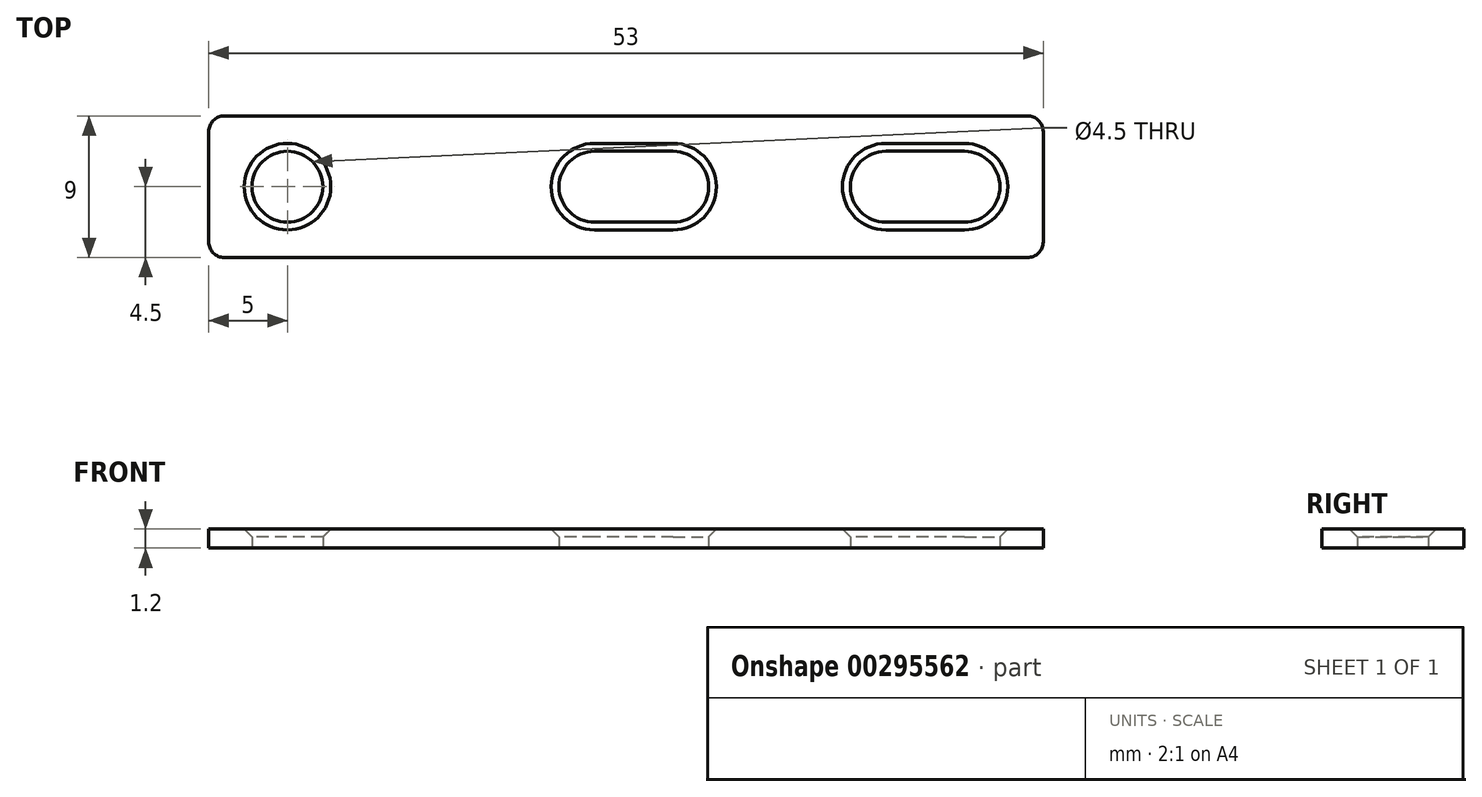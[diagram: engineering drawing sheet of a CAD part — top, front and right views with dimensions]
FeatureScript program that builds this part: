
annotation { "Feature Type Name" : "Feature", "Feature Type Description" : "" }
export const myFeature = defineFeature(function(context is Context, id is Id, definition is map)
    precondition{}
    {
        {
            var Q0;
            Q0=qCreatedBy(makeId("Top.planeOp"),FACE);
            var sketch = newSketch(context, id + "F0", { "sketchPlane" : qUnion([Q0])});
            skLineSegment(sketch, "E0.bottom", {"start": v(26.5, 4.5) * mm, "end": v(-26.5, 4.5) * mm});
            skLineSegment(sketch, "E0.top", {"start": v(26.5, -4.5) * mm, "end": v(-26.5, -4.5) * mm});
            skLineSegment(sketch, "E0.left", {"start": v(26.5, 4.5) * mm, "end": v(26.5, -4.5) * mm});
            skLineSegment(sketch, "E0.right", {"start": v(-26.5, 4.5) * mm, "end": v(-26.5, -4.5) * mm});
            skPoint(sketch, "E0.middle", {"position": v(0, 0) * mm});
            skCircle(sketch, "E1", {"center": v(-21.5, 0) * mm, "radius": 2.25 * mm});
            skPoint(sketch, "E1.centerSnap0", {"position": v(-26.5, 0) * mm});
            skLineSegment(sketch, "E2", {"start": v(-2, 0) * mm, "end": v(3, 0) * mm, "construction": true});
            skLineSegment(sketch, "E3", {"start": v(-26.5, 0) * mm, "end": v(-21.5, 0) * mm, "construction": true});
            skLineSegment(sketch, "E4", {"start": v(-2, 0) * mm, "end": v(-21.5, 0) * mm, "construction": true});
            skArc(sketch, "E5.0.startCap", {"start": v(-2, -2.25) * mm, "mid": v(-4.25, 0) * mm, "end": v(-2, 2.25) * mm});
            skArc(sketch, "E5.0.endCap", {"start": v(3, 2.25) * mm, "mid": v(5.25, 0) * mm, "end": v(3, -2.25) * mm});
            skLineSegment(sketch, "E5.0.left", {"start": v(-2, 2.25) * mm, "end": v(3, 2.25) * mm});
            skLineSegment(sketch, "E5.0.right", {"start": v(-2, -2.25) * mm, "end": v(3, -2.25) * mm});
            skLineSegment(sketch, "E6", {"start": v(3, 0) * mm, "end": v(16.5, 0) * mm, "construction": true});
            skLineSegment(sketch, "E7", {"start": v(16.5, 0) * mm, "end": v(21.5, 0) * mm, "construction": true});
            skArc(sketch, "E8.0.startCap", {"start": v(16.5, -2.25) * mm, "mid": v(14.25, 0) * mm, "end": v(16.5, 2.25) * mm});
            skArc(sketch, "E8.0.endCap", {"start": v(21.5, 2.25) * mm, "mid": v(23.75, 0) * mm, "end": v(21.5, -2.25) * mm});
            skLineSegment(sketch, "E8.0.left", {"start": v(16.5, 2.25) * mm, "end": v(21.5, 2.25) * mm});
            skLineSegment(sketch, "E8.0.right", {"start": v(16.5, -2.25) * mm, "end": v(21.5, -2.25) * mm});
            skSolve(sketch);
        }
        {
            var Q0;
            Q0=makeQuery(id+"F0.imprint","IMPRINT",FACE,{"disambiguationData":[TD([[makeQuery(id+"F0.imprint","IMPRINT",EDGE,{"derivedFrom":sQuery(id+"F0.wireOp",EDGE,"E0.bottom")}),1.0]])]});
            extrude(context, id + "F1", {"entities" : qUnion([Q0]), "depth" : 1.2 * mm});
        }
        {
            var Q0;
            Q0=makeQuery(id+"F1.opExtrude","SWEPT_EDGE",EDGE,{"disambiguationData":[OSD([sQuery(id+"F0.wireOp",EDGE,"E0.top"),sQuery(id+"F0.wireOp",EDGE,"E0.right")])]});
            var Q1;
            Q1=makeQuery(id+"F1.opExtrude","SWEPT_EDGE",EDGE,{"disambiguationData":[OSD([sQuery(id+"F0.wireOp",EDGE,"E0.bottom"),sQuery(id+"F0.wireOp",EDGE,"E0.right")])]});
            var Q2;
            Q2=makeQuery(id+"F1.opExtrude","SWEPT_EDGE",EDGE,{"disambiguationData":[OSD([sQuery(id+"F0.wireOp",EDGE,"E0.top"),sQuery(id+"F0.wireOp",EDGE,"E0.left")])]});
            var Q3;
            Q3=makeQuery(id+"F1.opExtrude","SWEPT_EDGE",EDGE,{"disambiguationData":[OSD([sQuery(id+"F0.wireOp",EDGE,"E0.bottom"),sQuery(id+"F0.wireOp",EDGE,"E0.left")])]});
            fillet(context, id + "F2", {"entities" : qUnion([Q0, Q1, Q2, Q3]), "radius" : 1 * mm, "tangentPropagation" : true, "allowEdgeOverflow" : false});
        }
        {
            var Q0;
            Q0=makeQuery(id+"F1.opExtrude","CAP_EDGE",EDGE,{"disambiguationData":[OSD([sQuery(id+"F0.wireOp",EDGE,"E1")])],"isStart":false});
            var Q1;
            Q1=makeQuery(id+"F1.opExtrude","CAP_EDGE",EDGE,{"disambiguationData":[OSD([sQuery(id+"F0.wireOp",EDGE,"E5.0.startCap")])],"isStart":false});
            var Q2;
            Q2=makeQuery(id+"F1.opExtrude","CAP_EDGE",EDGE,{"disambiguationData":[OSD([sQuery(id+"F0.wireOp",EDGE,"E8.0.startCap")])],"isStart":false});
            chamfer(context, id + "F3", {"entities" : qUnion([Q0, Q1, Q2]), "width" : 0.5 * mm, "tangentPropagation" : true});
        }
    });
